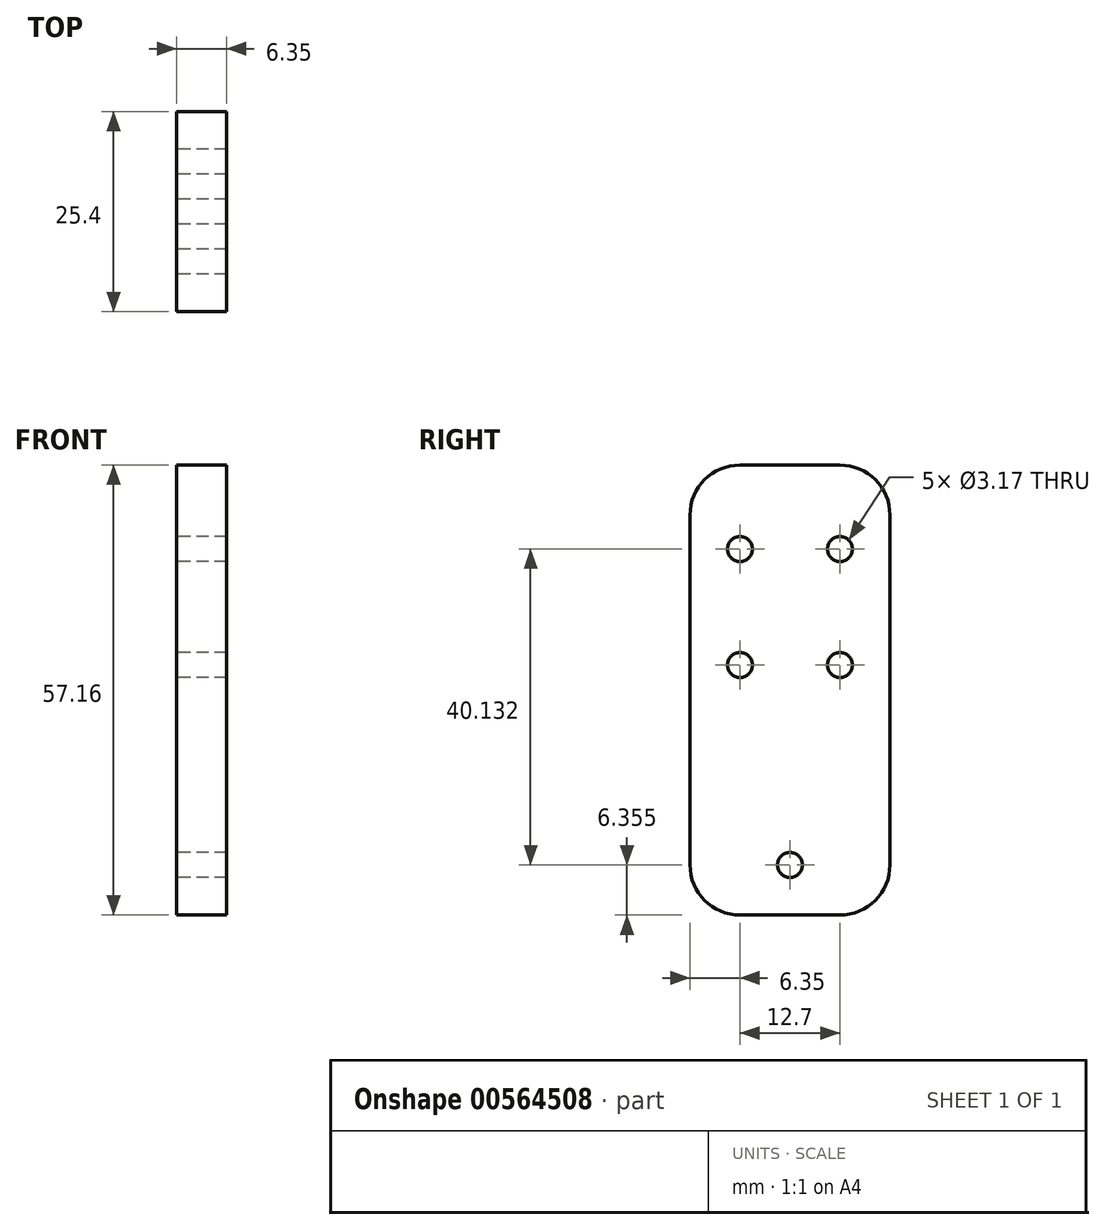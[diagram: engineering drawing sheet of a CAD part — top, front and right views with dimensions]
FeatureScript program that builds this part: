
annotation { "Feature Type Name" : "Feature", "Feature Type Description" : "" }
export const myFeature = defineFeature(function(context is Context, id is Id, definition is map)
    precondition{}
    {
        {
            var Q0;
            Q0=qCreatedBy(makeId("Right.planeOp"),FACE);
            var sketch = newSketch(context, id + "F0", { "sketchPlane" : qUnion([Q0])});
            skLineSegment(sketch, "E0.bottom", {"start": v(12.7, 28.58) * mm, "end": v(-12.7, 28.57) * mm});
            skLineSegment(sketch, "E0.top", {"start": v(12.7, -28.57) * mm, "end": v(-12.7, -28.58) * mm});
            skLineSegment(sketch, "E0.left", {"start": v(12.7, 28.58) * mm, "end": v(12.7, -28.57) * mm});
            skLineSegment(sketch, "E0.right", {"start": v(-12.7, 28.57) * mm, "end": v(-12.7, -28.58) * mm});
            skPoint(sketch, "E0.middle", {"position": v(0, 0) * mm});
            skCircle(sketch, "E1", {"center": v(0, -22.23) * mm, "radius": 1.59 * mm});
            skCircle(sketch, "E2", {"center": v(-6.35, 17.9) * mm, "radius": 1.59 * mm});
            skCircle(sketch, "E3", {"center": v(6.35, 17.9) * mm, "radius": 1.59 * mm});
            skCircle(sketch, "E4", {"center": v(6.35, 3.17) * mm, "radius": 1.59 * mm});
            skCircle(sketch, "E5", {"center": v(-6.35, 3.17) * mm, "radius": 1.59 * mm});
            skSolve(sketch);
        }
        {
            var Q0;
            Q0=makeQuery(id+"F0.imprint","IMPRINT",FACE,{"disambiguationData":[TD([[makeQuery(id+"F0.imprint","IMPRINT",EDGE,{"derivedFrom":sQuery(id+"F0.wireOp",EDGE,"E0.bottom")}),1.0]])]});
            extrude(context, id + "F1", {"entities" : qUnion([Q0]), "depth" : 6.35 * mm, "offsetDistance" : 25.4 * mm});
        }
        {
            var Q0;
            Q0=makeQuery(id+"F1.opExtrude","SWEPT_EDGE",EDGE,{"disambiguationData":[OSD([sQuery(id+"F0.wireOp",EDGE,"E0.bottom"),sQuery(id+"F0.wireOp",EDGE,"E0.right")])]});
            var Q1;
            Q1=makeQuery(id+"F1.opExtrude","SWEPT_EDGE",EDGE,{"disambiguationData":[OSD([sQuery(id+"F0.wireOp",EDGE,"E0.bottom"),sQuery(id+"F0.wireOp",EDGE,"E0.left")])]});
            fillet(context, id + "F2", {"entities" : qUnion([Q0, Q1]), "radius" : 6.35 * mm, "tangentPropagation" : true, "allowEdgeOverflow" : false});
        }
        {
            var Q0;
            Q0=makeQuery(id+"F1.opExtrude","SWEPT_EDGE",EDGE,{"disambiguationData":[OSD([sQuery(id+"F0.wireOp",EDGE,"E0.top"),sQuery(id+"F0.wireOp",EDGE,"E0.right")])]});
            var Q1;
            Q1=makeQuery(id+"F1.opExtrude","SWEPT_EDGE",EDGE,{"disambiguationData":[OSD([sQuery(id+"F0.wireOp",EDGE,"E0.top"),sQuery(id+"F0.wireOp",EDGE,"E0.left")])]});
            fillet(context, id + "F3", {"entities" : qUnion([Q0, Q1]), "radius" : 6.35 * mm, "tangentPropagation" : true, "allowEdgeOverflow" : false});
        }
    });
